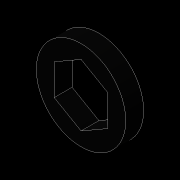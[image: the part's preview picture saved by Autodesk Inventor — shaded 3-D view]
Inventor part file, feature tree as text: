
AUTODESK INVENTOR PART (.ipt)
format: ipt  version: 2016 (Build 200138000, 138)  size: 80,896 bytes
history: native  units: in
note: dims shown in document units (in); Inventor stores cm internally (conversion verified against a paired STEP export)
features: extrude x1, sketch x1
ambient origin geometry x8: Origin, YZ Plane, XZ Plane, XY Plane, X Axis, Y Axis, Z Axis, Center Point
bodies: Solid1 (feature_tree)
feature tree (2):
  extrude  "Extrusion1"  Depth=0.125in
  sketch  "Sketch1"  dims[d0=0.375in d1=0.625in d2=0.125in d3=0.0in]
